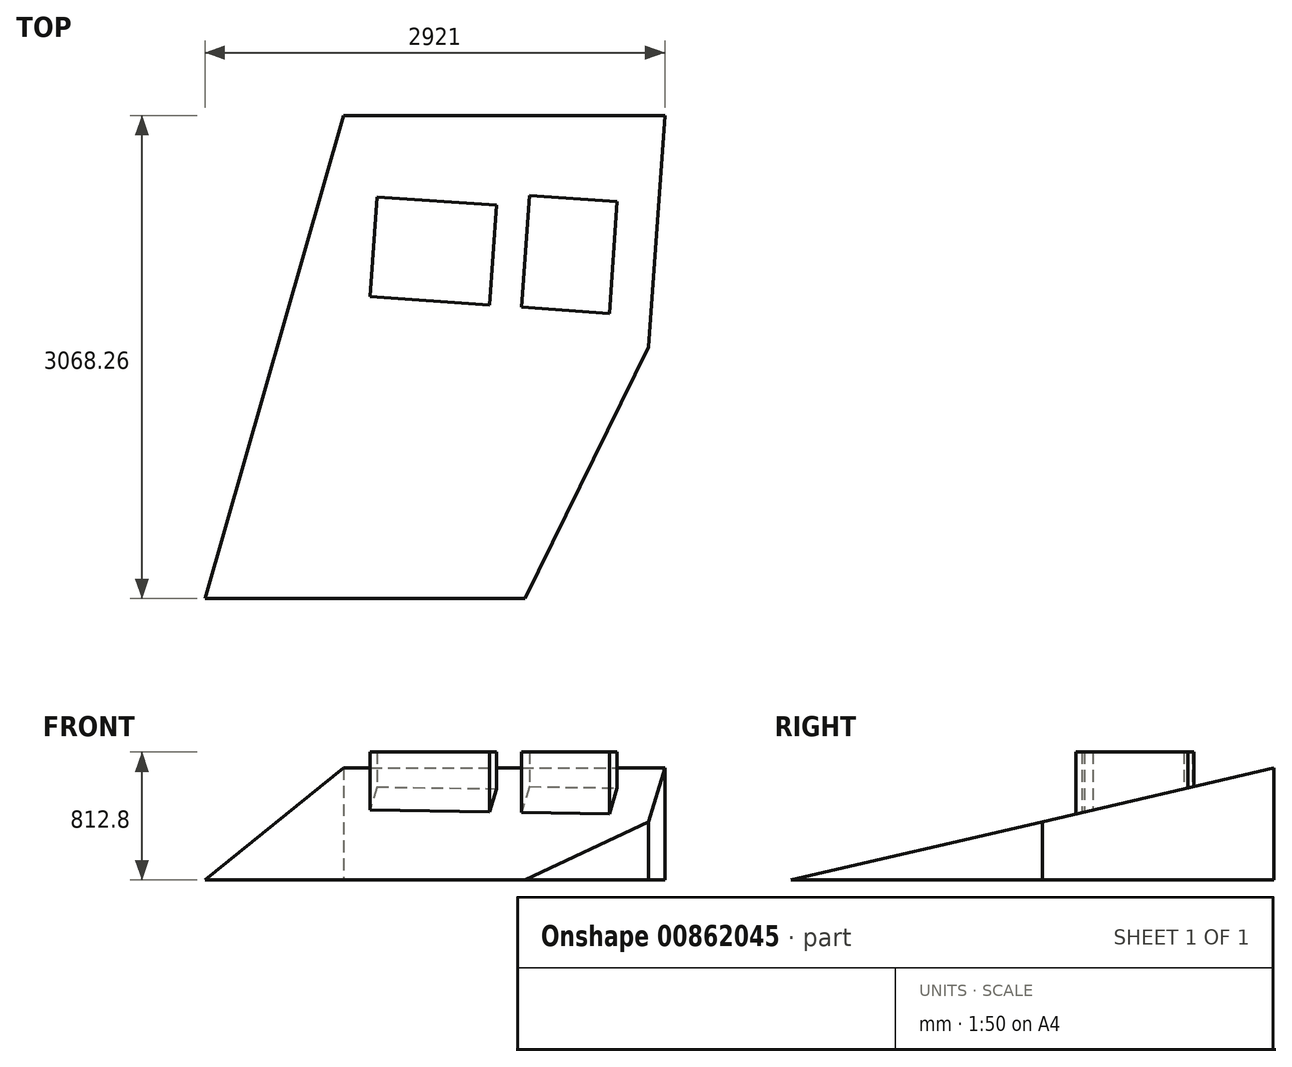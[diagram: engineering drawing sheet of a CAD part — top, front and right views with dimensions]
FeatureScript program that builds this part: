
annotation { "Feature Type Name" : "Feature", "Feature Type Description" : "" }
export const myFeature = defineFeature(function(context is Context, id is Id, definition is map)
    precondition{}
    {
        {
            var Q0;
            Q0=qCreatedBy(makeId("Right.planeOp"),FACE);
            var sketch = newSketch(context, id + "F0", { "sketchPlane" : qUnion([Q0])});
            skLineSegment(sketch, "E0", {"start": v(0, 0) * mm, "end": v(-1534.13, -355.6) * mm});
            skLineSegment(sketch, "E1", {"start": v(0, 0) * mm, "end": v(1534.13, 355.6) * mm});
            skLineSegment(sketch, "E2", {"start": v(-1534.13, -355.6) * mm, "end": v(1534.13, -355.6) * mm});
            skLineSegment(sketch, "E3", {"start": v(1534.13, -355.6) * mm, "end": v(1534.13, 355.6) * mm});
            skSolve(sketch);
        }
        {
            var Q0;
            Q0=makeQuery(id+"F0.imprint","IMPRINT",FACE,{"disambiguationData":[TD([[makeQuery(id+"F0.imprint","IMPRINT",EDGE,{"derivedFrom":sQuery(id+"F0.wireOp",EDGE,"E0")}),1.0]])]});
            extrude(context, id + "F1", {"entities" : qUnion([Q0]), "endBound" : BoundingType.SYMMETRIC, "oppositeDirection" : true, "depth" : 2921 * mm, "offsetDistance" : 25.4 * mm});
        }
        {
            var Q0;
            Q0=makeQuery(id+"F1.opExtrude","SWEPT_FACE",FACE,{"disambiguationData":[OSD([sQuery(id+"F0.wireOp",EDGE,"E2")])]});
            var sketch = newSketch(context, id + "F2", { "sketchPlane" : qUnion([Q0])});
            skLineSegment(sketch, "E4", {"start": v(-1460.5, 1534.13) * mm, "end": v(-580.7, -1534.13) * mm});
            skLineSegment(sketch, "E5", {"start": v(-1460.5, 1534.13) * mm, "end": v(-1460.5, -1534.13) * mm});
            skLineSegment(sketch, "E6", {"start": v(-1460.5, -1534.13) * mm, "end": v(-580.7, -1534.13) * mm});
            skLineSegment(sketch, "E7", {"start": v(1460.5, 1534.13) * mm, "end": v(571.5, 1534.13) * mm});
            skLineSegment(sketch, "E8", {"start": v(571.5, 1534.13) * mm, "end": v(1357.73, -64.51) * mm});
            skLineSegment(sketch, "E9", {"start": v(1460.5, -1534.13) * mm, "end": v(1357.73, -64.51) * mm});
            skLineSegment(sketch, "E10", {"start": v(1460.5, -1534.13) * mm, "end": v(1460.5, 1534.13) * mm});
            skSolve(sketch);
        }
        {
            var Q0;
            Q0=qSketchRegion(id+"F2",true);
            extrude(context, id + "F3", {"entities" : qUnion([Q0]), "operationType" : NewBodyOperationType.REMOVE, "endBound" : BoundingType.THROUGH_ALL, "oppositeDirection" : true, "depth" : 25.4 * mm, "offsetDistance" : 25.4 * mm});
        }
        {
            var Q0;
            Q0=makeQuery(id+"F1.opExtrude","SWEPT_FACE",FACE,{"disambiguationData":[OSD([sQuery(id+"F0.wireOp",EDGE,"E2")])]});
            var sketch = newSketch(context, id + "F4", { "sketchPlane" : qUnion([Q0])});
            skLineSegment(sketch, "E11.bottom", {"start": v(-367, -1017.44) * mm, "end": v(393.14, -964.29) * mm});
            skLineSegment(sketch, "E11.left", {"start": v(-367, -1017.44) * mm, "end": v(-411.3, -383.99) * mm});
            skLineSegment(sketch, "E11.right", {"start": v(393.14, -964.29) * mm, "end": v(348.85, -330.83) * mm});
            skLineSegment(sketch, "E12", {"start": v(-367, -1017.44) * mm, "end": v(-721.74, -1042.25) * mm, "construction": true});
            skLineSegment(sketch, "E13.bottom", {"start": v(601.16, -1026.13) * mm, "end": v(1158.6, -987.15) * mm});
            skLineSegment(sketch, "E13.top", {"start": v(551.55, -316.66) * mm, "end": v(1108.99, -277.68) * mm});
            skLineSegment(sketch, "E13.left", {"start": v(601.16, -1026.13) * mm, "end": v(551.55, -316.66) * mm});
            skLineSegment(sketch, "E13.right", {"start": v(1158.6, -987.15) * mm, "end": v(1108.99, -277.68) * mm});
            skLineSegment(sketch, "E14", {"start": v(-411.3, -383.99) * mm, "end": v(348.85, -330.83) * mm});
            skLineSegment(sketch, "E15", {"start": v(551.55, -316.66) * mm, "end": v(348.85, -330.83) * mm, "construction": true});
            skLineSegment(sketch, "E16", {"start": v(601.16, -1026.13) * mm, "end": v(601.16, -1534.13) * mm, "construction": true});
            skSolve(sketch);
        }
        {
            var Q0;
            Q0 = qSketchRegion(id + "F4", true);
            extrude(context, id + "F5", {"entities" : qUnion([Q0]), "operationType" : NewBodyOperationType.ADD, "oppositeDirection" : true, "depth" : 812.8 * mm, "offsetDistance" : 25.4 * mm});
        }
    });
